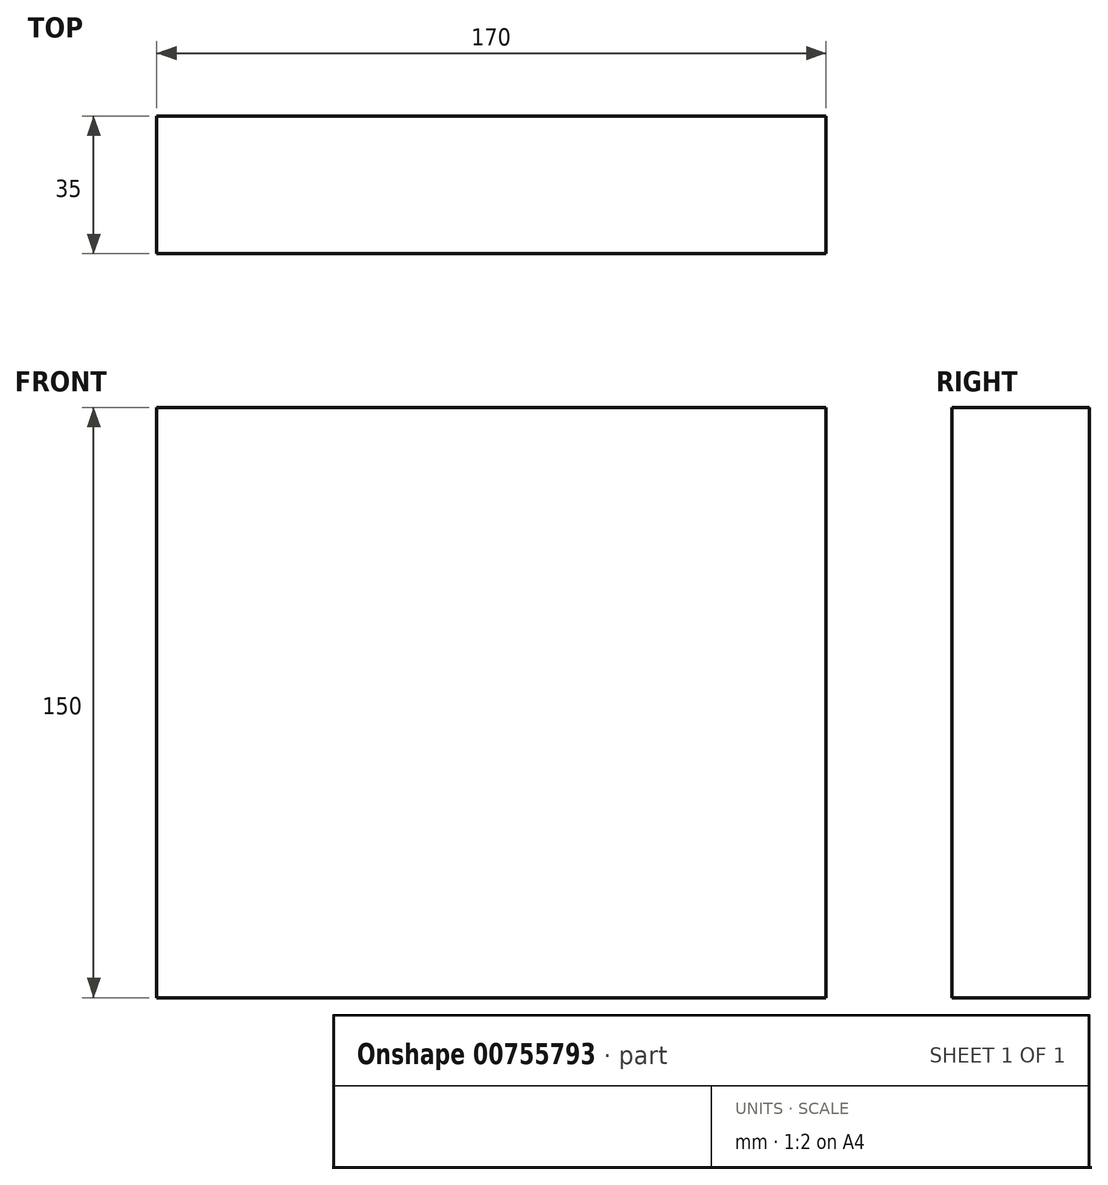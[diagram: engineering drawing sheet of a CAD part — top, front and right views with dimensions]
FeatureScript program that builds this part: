
annotation { "Feature Type Name" : "Feature", "Feature Type Description" : "" }
export const myFeature = defineFeature(function(context is Context, id is Id, definition is map)
    precondition{}
    {
        {
            var Q0;
            Q0=qCreatedBy(makeId("Top.planeOp"),FACE);
            var sketch = newSketch(context, id + "F0", { "sketchPlane" : qUnion([Q0])});
            skLineSegment(sketch, "E0.bottom", {"start": v(85, 17.5) * mm, "end": v(-85, 17.5) * mm});
            skLineSegment(sketch, "E0.top", {"start": v(85, -17.5) * mm, "end": v(-85, -17.5) * mm});
            skLineSegment(sketch, "E0.left", {"start": v(85, 17.5) * mm, "end": v(85, -17.5) * mm});
            skLineSegment(sketch, "E0.right", {"start": v(-85, 17.5) * mm, "end": v(-85, -17.5) * mm});
            skPoint(sketch, "E0.middle", {"position": v(0, 0) * mm});
            skSolve(sketch);
        }
        {
            var Q0;
            Q0=makeQuery(id+"F0.imprint","IMPRINT",FACE,{"disambiguationData":[TD([[makeQuery(id+"F0.imprint","IMPRINT",EDGE,{"derivedFrom":sQuery(id+"F0.wireOp",EDGE,"E0.bottom")}),1.0]])]});
            extrude(context, id + "F1", {"entities" : qUnion([Q0]), "depth" : 150 * mm, "offsetDistance" : 25 * mm});
        }
    });
